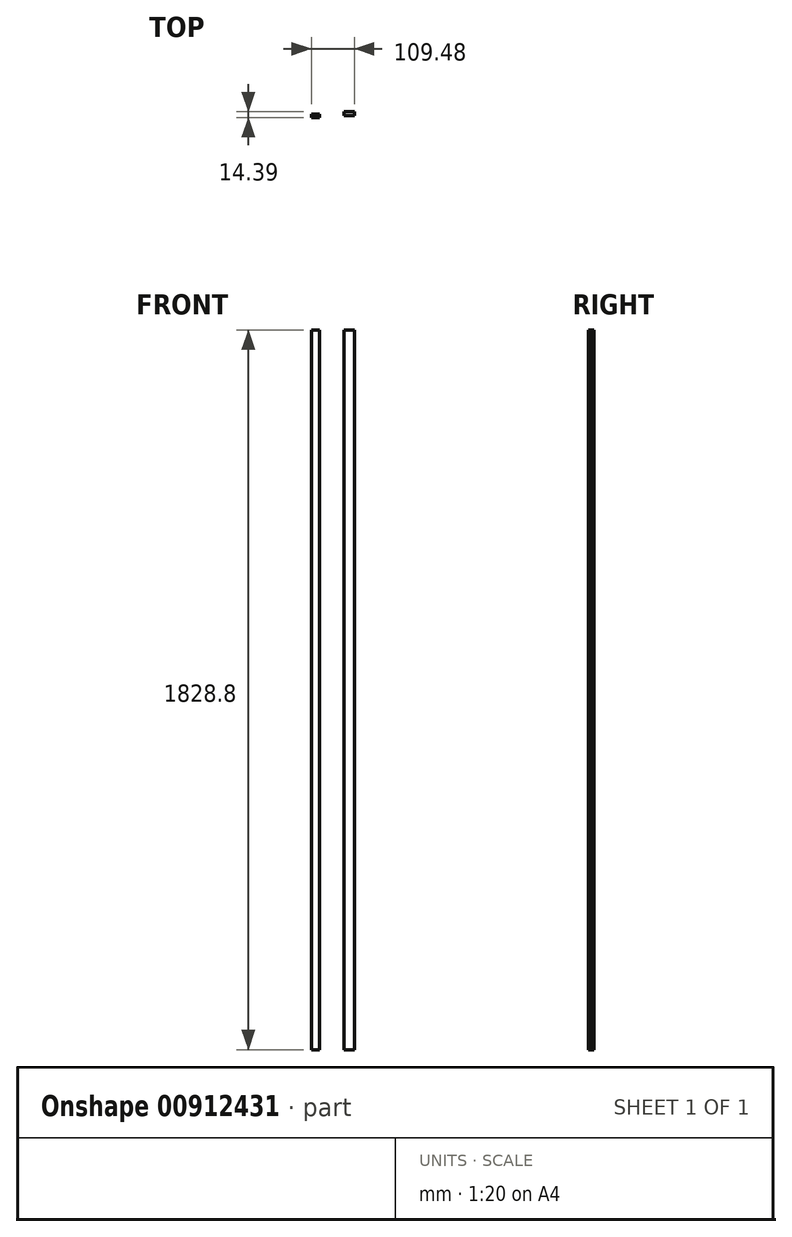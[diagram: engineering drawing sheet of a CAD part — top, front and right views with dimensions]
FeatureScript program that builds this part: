
annotation { "Feature Type Name" : "Feature", "Feature Type Description" : "" }
export const myFeature = defineFeature(function(context is Context, id is Id, definition is map)
    precondition{}
    {
        {
            var Q0;
            Q0=qCreatedBy(makeId("Top.planeOp"),FACE);
            var sketch = newSketch(context, id + "F0", { "sketchPlane" : qUnion([Q0])});
            skLineSegment(sketch, "E0.bottom", {"start": v(-41.7, 29.55) * mm, "end": v(-62.54, 29.55) * mm});
            skLineSegment(sketch, "E0.top", {"start": v(-41.7, 38.1) * mm, "end": v(-62.54, 38.1) * mm});
            skLineSegment(sketch, "E0.left", {"start": v(-41.7, 29.55) * mm, "end": v(-41.7, 38.1) * mm});
            skLineSegment(sketch, "E0.right", {"start": v(-62.54, 29.55) * mm, "end": v(-62.54, 38.1) * mm});
            skLineSegment(sketch, "E1.bottom", {"start": v(21.15, 34.8) * mm, "end": v(46.94, 34.8) * mm});
            skLineSegment(sketch, "E1.top", {"start": v(21.15, 43.94) * mm, "end": v(46.94, 43.94) * mm});
            skLineSegment(sketch, "E1.left", {"start": v(21.15, 34.8) * mm, "end": v(21.15, 43.94) * mm});
            skLineSegment(sketch, "E1.right", {"start": v(46.94, 34.8) * mm, "end": v(46.94, 43.94) * mm});
            skLineSegment(sketch, "E2.bottom", {"start": v(-63.14, -25.2) * mm, "end": v(-42.9, -25.2) * mm});
            skLineSegment(sketch, "E2.top", {"start": v(-63.14, -32.55) * mm, "end": v(-42.9, -32.55) * mm});
            skLineSegment(sketch, "E2.left", {"start": v(-63.14, -25.2) * mm, "end": v(-63.14, -32.55) * mm});
            skLineSegment(sketch, "E2.right", {"start": v(-42.9, -25.2) * mm, "end": v(-42.9, -32.55) * mm});
            skLineSegment(sketch, "E3.bottom", {"start": v(24.3, -19.65) * mm, "end": v(53.4, -19.65) * mm});
            skLineSegment(sketch, "E3.top", {"start": v(24.3, -30) * mm, "end": v(53.4, -30) * mm});
            skLineSegment(sketch, "E3.left", {"start": v(24.3, -19.65) * mm, "end": v(24.3, -30) * mm});
            skLineSegment(sketch, "E3.right", {"start": v(53.4, -19.65) * mm, "end": v(53.4, -30) * mm});
            skSolve(sketch);
        }
        {
            var Q0;
            Q0=makeQuery(id+"F0.imprint","IMPRINT",FACE,{"disambiguationData":[TD([[makeQuery(id+"F0.imprint","IMPRINT",EDGE,{"derivedFrom":sQuery(id+"F0.wireOp",EDGE,"E0.bottom")}),-1.0]])]});
            var Q1;
            Q1=makeQuery(id+"F0.imprint","IMPRINT",FACE,{"disambiguationData":[TD([[makeQuery(id+"F0.imprint","IMPRINT",EDGE,{"derivedFrom":sQuery(id+"F0.wireOp",EDGE,"E1.bottom")}),1.0]])]});
            extrude(context, id + "F1", {"entities" : qUnion([Q0, Q1]), "depth" : 1828.8 * mm, "offsetDistance" : 25.4 * mm});
        }
    });
